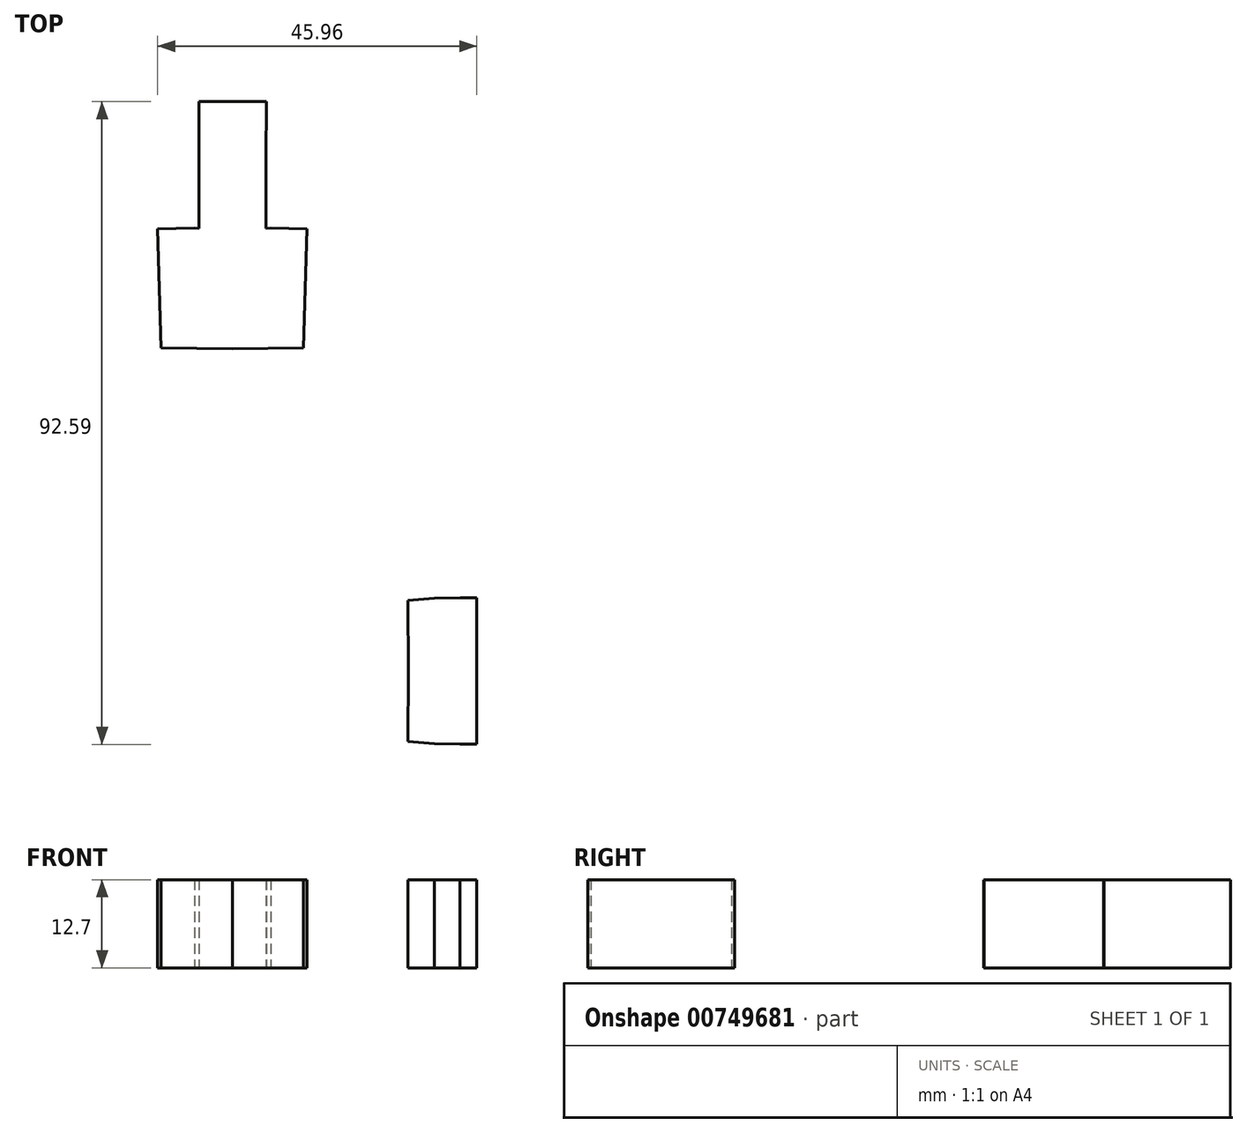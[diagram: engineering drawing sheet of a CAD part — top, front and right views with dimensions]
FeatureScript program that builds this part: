
annotation { "Feature Type Name" : "Feature", "Feature Type Description" : "" }
export const myFeature = defineFeature(function(context is Context, id is Id, definition is map)
    precondition{}
    {
        {
            var Q0;
            Q0=qCreatedBy(makeId("Top.planeOp"),FACE);
            var sketch = newSketch(context, id + "F0", { "sketchPlane" : qUnion([Q0])});
            skLineSegment(sketch, "E0", {"start": v(-36.51, 121.34) * mm, "end": v(-36.27, 119.16) * mm});
            skLineSegment(sketch, "E1", {"start": v(-36.07, 123.48) * mm, "end": v(-36.51, 121.34) * mm});
            skLineSegment(sketch, "E2", {"start": v(-29.86, 114.03) * mm, "end": v(-27.69, 114.27) * mm});
            skLineSegment(sketch, "E3", {"start": v(-27.69, 114.27) * mm, "end": v(-25.7, 115.16) * mm});
            skLineSegment(sketch, "E4", {"start": v(-33.9, 115.55) * mm, "end": v(-32, 114.47) * mm});
            skLineSegment(sketch, "E5", {"start": v(-32, 114.47) * mm, "end": v(-29.86, 114.03) * mm});
            skLineSegment(sketch, "E6", {"start": v(-25.16, 126.46) * mm, "end": v(-27.06, 127.54) * mm});
            skLineSegment(sketch, "E7", {"start": v(-27.06, 127.54) * mm, "end": v(-29.2, 127.99) * mm});
            skLineSegment(sketch, "E8", {"start": v(-22.8, 122.85) * mm, "end": v(-23.69, 124.84) * mm});
            skLineSegment(sketch, "E9", {"start": v(-23.69, 124.84) * mm, "end": v(-25.16, 126.46) * mm});
            skLineSegment(sketch, "E10", {"start": v(-33.37, 126.85) * mm, "end": v(-34.98, 125.38) * mm});
            skLineSegment(sketch, "E11", {"start": v(-34.98, 125.38) * mm, "end": v(-36.07, 123.48) * mm});
            skLineSegment(sketch, "E12", {"start": v(-29.2, 127.99) * mm, "end": v(-31.37, 127.75) * mm});
            skLineSegment(sketch, "E13", {"start": v(-31.37, 127.75) * mm, "end": v(-33.37, 126.85) * mm});
            skLineSegment(sketch, "E14", {"start": v(-23, 118.53) * mm, "end": v(-22.55, 120.67) * mm});
            skLineSegment(sketch, "E15", {"start": v(-22.55, 120.67) * mm, "end": v(-22.8, 122.85) * mm});
            skLineSegment(sketch, "E16", {"start": v(-25.7, 115.16) * mm, "end": v(-24.08, 116.64) * mm});
            skLineSegment(sketch, "E17", {"start": v(-24.08, 116.64) * mm, "end": v(-23, 118.53) * mm});
            skLineSegment(sketch, "E18", {"start": v(-36.27, 119.16) * mm, "end": v(-35.37, 117.17) * mm});
            skLineSegment(sketch, "E19", {"start": v(-35.37, 117.17) * mm, "end": v(-33.9, 115.55) * mm});
            skLineSegment(sketch, "E20", {"start": v(-21.43, 123.46) * mm, "end": v(-22.32, 125.46) * mm});
            skLineSegment(sketch, "E21", {"start": v(-20.53, 121.47) * mm, "end": v(-21.43, 123.46) * mm});
            skLineSegment(sketch, "E22", {"start": v(-19.9, 119.28) * mm, "end": v(-20.53, 121.47) * mm});
            skLineSegment(sketch, "E23", {"start": v(-39.23, 123.54) * mm, "end": v(-40.65, 122.6) * mm});
            skLineSegment(sketch, "E24", {"start": v(-57.32, -66.74) * mm, "end": v(-57.32, -74.04) * mm});
            skLineSegment(sketch, "E25", {"start": v(-57.32, -74.04) * mm, "end": v(-57.32, -81.34) * mm});
            skLineSegment(sketch, "E26", {"start": v(-57.32, -81.34) * mm, "end": v(-50.68, -80.7) * mm});
            skLineSegment(sketch, "E27", {"start": v(-39.13, -68.41) * mm, "end": v(-50.68, -67.38) * mm});
            skLineSegment(sketch, "E28", {"start": v(-50.68, -67.38) * mm, "end": v(-57.32, -66.74) * mm});
            skLineSegment(sketch, "E29", {"start": v(-50.68, -80.7) * mm, "end": v(-39.38, -79.55) * mm});
            skLineSegment(sketch, "E30", {"start": v(-40.45, -82.84) * mm, "end": v(-39.38, -79.55) * mm});
            skLineSegment(sketch, "E31", {"start": v(-51.06, -83.72) * mm, "end": v(-40.45, -82.84) * mm});
            skLineSegment(sketch, "E32", {"start": v(-57.32, -81.34) * mm, "end": v(-57.63, -84.23) * mm});
            skLineSegment(sketch, "E33", {"start": v(-57.63, -63.85) * mm, "end": v(-57.32, -66.74) * mm});
            skLineSegment(sketch, "E34", {"start": v(-40.45, -65.23) * mm, "end": v(-51.06, -64.36) * mm});
            skLineSegment(sketch, "E35", {"start": v(-39.13, -68.41) * mm, "end": v(-40.45, -65.23) * mm});
            skLineSegment(sketch, "E36", {"start": v(-41.05, -87.72) * mm, "end": v(-39.4, -84.97) * mm});
            skLineSegment(sketch, "E37", {"start": v(-39.4, -84.97) * mm, "end": v(-40.45, -82.84) * mm});
            skLineSegment(sketch, "E38", {"start": v(-51.43, -85.25) * mm, "end": v(-41.05, -87.72) * mm});
            skLineSegment(sketch, "E39", {"start": v(-57.63, -84.2) * mm, "end": v(-51.43, -85.25) * mm});
            skLineSegment(sketch, "E40", {"start": v(-51.06, -83.72) * mm, "end": v(-57.63, -84.2) * mm});
            skLineSegment(sketch, "E41", {"start": v(-40.45, -65.23) * mm, "end": v(-39.4, -63.1) * mm});
            skLineSegment(sketch, "E42", {"start": v(-39.4, -63.1) * mm, "end": v(-41.05, -60.35) * mm});
            skLineSegment(sketch, "E43", {"start": v(-41.05, -60.35) * mm, "end": v(-51.43, -62.82) * mm});
            skLineSegment(sketch, "E44", {"start": v(-57.63, -63.88) * mm, "end": v(-51.06, -64.36) * mm});
            skLineSegment(sketch, "E45", {"start": v(-51.43, -62.82) * mm, "end": v(-57.63, -63.88) * mm});
            skLineSegment(sketch, "E46", {"start": v(-36.61, -76.89) * mm, "end": v(-37.07, -74.03) * mm});
            skLineSegment(sketch, "E47", {"start": v(-33.46, -77.71) * mm, "end": v(-36.61, -76.89) * mm});
            skLineSegment(sketch, "E48", {"start": v(-24.1, -74.32) * mm, "end": v(-24.17, -77.93) * mm});
            skLineSegment(sketch, "E49", {"start": v(-33.5, -79.68) * mm, "end": v(-22.06, -79.95) * mm});
            skLineSegment(sketch, "E50", {"start": v(-24.17, -77.93) * mm, "end": v(-33.46, -77.71) * mm});
            skLineSegment(sketch, "E51", {"start": v(-37.07, -74.03) * mm, "end": v(-36.48, -71.2) * mm});
            skLineSegment(sketch, "E52", {"start": v(-36.48, -71.2) * mm, "end": v(-33.3, -70.51) * mm});
            skLineSegment(sketch, "E53", {"start": v(-24, -70.72) * mm, "end": v(-24.1, -74.32) * mm});
            skLineSegment(sketch, "E54", {"start": v(-33.3, -70.51) * mm, "end": v(-24, -70.72) * mm});
            skLineSegment(sketch, "E55", {"start": v(-21.8, -68.8) * mm, "end": v(-33.25, -68.54) * mm});
            skLineSegment(sketch, "E56", {"start": v(-39.38, -79.55) * mm, "end": v(-37.63, -82.46) * mm});
            skLineSegment(sketch, "E57", {"start": v(-20.94, -91.92) * mm, "end": v(-23.48, -82.8) * mm});
            skLineSegment(sketch, "E58", {"start": v(-35.26, -82.54) * mm, "end": v(-28.7, -91.67) * mm});
            skLineSegment(sketch, "E59", {"start": v(-37.63, -82.46) * mm, "end": v(-35.26, -82.54) * mm});
            skLineSegment(sketch, "E60", {"start": v(-23.48, -82.8) * mm, "end": v(-22.06, -79.95) * mm});
            skLineSegment(sketch, "E61", {"start": v(-37.25, -65.58) * mm, "end": v(-39.13, -68.4) * mm});
            skLineSegment(sketch, "E62", {"start": v(-23.1, -65.87) * mm, "end": v(-20.15, -56.89) * mm});
            skLineSegment(sketch, "E63", {"start": v(-27.92, -56.79) * mm, "end": v(-34.87, -65.6) * mm});
            skLineSegment(sketch, "E64", {"start": v(-34.87, -65.6) * mm, "end": v(-37.25, -65.58) * mm});
            skLineSegment(sketch, "E65", {"start": v(-20.15, -56.89) * mm, "end": v(-27.92, -56.79) * mm});
            skLineSegment(sketch, "E66", {"start": v(-21.8, -68.8) * mm, "end": v(-23.1, -65.87) * mm});
            skLineSegment(sketch, "E67", {"start": v(-26.5, -43.73) * mm, "end": v(-27.92, -56.79) * mm});
            skLineSegment(sketch, "E68", {"start": v(-25.3, -32.83) * mm, "end": v(-26.5, -43.73) * mm});
            skLineSegment(sketch, "E69", {"start": v(-28.7, -91.67) * mm, "end": v(-27.88, -104.78) * mm});
            skLineSegment(sketch, "E70", {"start": v(-21.6, -106.6) * mm, "end": v(-20.94, -91.92) * mm});
            skLineSegment(sketch, "E71", {"start": v(-22.05, -116.27) * mm, "end": v(-21.6, -106.6) * mm});
            skLineSegment(sketch, "E72", {"start": v(-27.88, -104.78) * mm, "end": v(-27.18, -115.72) * mm});
            skLineSegment(sketch, "E73", {"start": v(-28.91, -126.27) * mm, "end": v(-23.98, -129.47) * mm});
            skLineSegment(sketch, "E74", {"start": v(-23.98, -129.47) * mm, "end": v(-22.05, -116.27) * mm});
            skLineSegment(sketch, "E75", {"start": v(-20.15, -42.2) * mm, "end": v(-20.14, -32.5) * mm});
            skLineSegment(sketch, "E76", {"start": v(-20.15, -56.89) * mm, "end": v(-20.15, -42.2) * mm});
            skLineSegment(sketch, "E77", {"start": v(-21.47, -19.24) * mm, "end": v(-26.55, -22.22) * mm});
            skLineSegment(sketch, "E78", {"start": v(-26.55, -22.22) * mm, "end": v(-25.3, -32.83) * mm});
            skLineSegment(sketch, "E79", {"start": v(-20.14, -32.5) * mm, "end": v(-21.47, -19.24) * mm});
            skLineSegment(sketch, "E80", {"start": v(-20.2, -66.03) * mm, "end": v(-21.8, -68.8) * mm});
            skLineSegment(sketch, "E81", {"start": v(-21.8, -68.8) * mm, "end": v(-13.28, -69.7) * mm});
            skLineSegment(sketch, "E82", {"start": v(-8.5, -69.93) * mm, "end": v(-13.28, -69.7) * mm});
            skLineSegment(sketch, "E83", {"start": v(-3.9, -70.15) * mm, "end": v(-8.5, -69.93) * mm});
            skLineSegment(sketch, "E84", {"start": v(-13.77, -79.86) * mm, "end": v(-8.99, -80.09) * mm});
            skLineSegment(sketch, "E85", {"start": v(-8.99, -80.09) * mm, "end": v(-4.39, -80.3) * mm});
            skLineSegment(sketch, "E86", {"start": v(-22.06, -79.95) * mm, "end": v(-13.77, -79.86) * mm});
            skLineSegment(sketch, "E87", {"start": v(-4.39, -80.3) * mm, "end": v(-4.14, -75.23) * mm});
            skLineSegment(sketch, "E88", {"start": v(-4.14, -75.23) * mm, "end": v(-3.9, -70.15) * mm});
            skLineSegment(sketch, "E89", {"start": v(-22.06, -79.95) * mm, "end": v(-21.01, -82.84) * mm});
            skLineSegment(sketch, "E90", {"start": v(-21.01, -82.84) * mm, "end": v(-14.18, -82.29) * mm});
            skLineSegment(sketch, "E91", {"start": v(-13.46, -67.24) * mm, "end": v(-20.2, -66.03) * mm});
            skLineSegment(sketch, "E92", {"start": v(-3.9, -70.15) * mm, "end": v(-3.76, -68.34) * mm});
            skLineSegment(sketch, "E93", {"start": v(-3.76, -68.34) * mm, "end": v(-8.26, -68) * mm});
            skLineSegment(sketch, "E94", {"start": v(-8.25, -68) * mm, "end": v(-13.46, -67.24) * mm});
            skLineSegment(sketch, "E95", {"start": v(-14.32, -82.26) * mm, "end": v(-8.92, -82.04) * mm});
            skLineSegment(sketch, "E96", {"start": v(-8.93, -82.04) * mm, "end": v(-4.42, -82.12) * mm});
            skLineSegment(sketch, "E97", {"start": v(-4.42, -82.12) * mm, "end": v(-4.39, -80.3) * mm});
            skLineSegment(sketch, "E98", {"start": v(37.47, -31.88) * mm, "end": v(29.33, -34.66) * mm});
            skLineSegment(sketch, "E99", {"start": v(21.15, -37.5) * mm, "end": v(17.9, -38.24) * mm});
            skLineSegment(sketch, "E100", {"start": v(19.54, -40.65) * mm, "end": v(20.83, -42.47) * mm});
            skLineSegment(sketch, "E101", {"start": v(29.33, -34.66) * mm, "end": v(21.15, -37.5) * mm});
            skLineSegment(sketch, "E102", {"start": v(30.83, -39.06) * mm, "end": v(38.98, -36.28) * mm});
            skLineSegment(sketch, "E103", {"start": v(20.83, -42.47) * mm, "end": v(30.83, -39.06) * mm});
            skLineSegment(sketch, "E104", {"start": v(1.77, -57.6) * mm, "end": v(1.1, -53.99) * mm});
            skLineSegment(sketch, "E105", {"start": v(8.75, -51.24) * mm, "end": v(8.5, -48.14) * mm});
            skLineSegment(sketch, "E106", {"start": v(1.1, -53.99) * mm, "end": v(4.13, -55.44) * mm});
            skLineSegment(sketch, "E107", {"start": v(4.13, -55.44) * mm, "end": v(8.75, -51.24) * mm});
            skLineSegment(sketch, "E108", {"start": v(11.25, -49.23) * mm, "end": v(20.83, -42.47) * mm});
            skLineSegment(sketch, "E109", {"start": v(17.9, -38.24) * mm, "end": v(6.8, -45.73) * mm});
            skLineSegment(sketch, "E110", {"start": v(8.5, -48.14) * mm, "end": v(11.25, -49.23) * mm});
            skLineSegment(sketch, "E111", {"start": v(6.8, -45.73) * mm, "end": v(-1.16, -51.27) * mm});
            skLineSegment(sketch, "E112", {"start": v(-1.16, -51.27) * mm, "end": v(-13.2, -59.66) * mm});
            skLineSegment(sketch, "E113", {"start": v(-7.17, -65.03) * mm, "end": v(-3.76, -68.34) * mm});
            skLineSegment(sketch, "E114", {"start": v(-3.76, -68.34) * mm, "end": v(-2.88, -61.83) * mm});
            skLineSegment(sketch, "E115", {"start": v(-13.46, -67.24) * mm, "end": v(-7.17, -65.03) * mm});
            skLineSegment(sketch, "E116", {"start": v(-2.88, -61.83) * mm, "end": v(1.77, -57.6) * mm});
            skLineSegment(sketch, "E117", {"start": v(19.54, -40.65) * mm, "end": v(17.85, -38.26) * mm});
            skLineSegment(sketch, "E118", {"start": v(38.98, -36.28) * mm, "end": v(38.28, -34.26) * mm});
            skLineSegment(sketch, "E119", {"start": v(38.28, -34.26) * mm, "end": v(37.47, -31.88) * mm});
            skLineSegment(sketch, "E120", {"start": v(17.57, -110.23) * mm, "end": v(16.11, -111.92) * mm});
            skLineSegment(sketch, "E121", {"start": v(14.2, -114.14) * mm, "end": v(17.42, -115.21) * mm});
            skLineSegment(sketch, "E122", {"start": v(17.42, -115.21) * mm, "end": v(25.28, -118.82) * mm});
            skLineSegment(sketch, "E123", {"start": v(25.28, -118.82) * mm, "end": v(33.12, -122.37) * mm});
            skLineSegment(sketch, "E124", {"start": v(34.16, -120.08) * mm, "end": v(35.04, -118.13) * mm});
            skLineSegment(sketch, "E125", {"start": v(33.12, -122.37) * mm, "end": v(34.16, -120.08) * mm});
            skLineSegment(sketch, "E126", {"start": v(27.2, -114.59) * mm, "end": v(17.57, -110.23) * mm});
            skLineSegment(sketch, "E127", {"start": v(35.04, -118.13) * mm, "end": v(27.2, -114.59) * mm});
            skLineSegment(sketch, "E128", {"start": v(-0.96, -96.88) * mm, "end": v(0.05, -93.35) * mm});
            skLineSegment(sketch, "E129", {"start": v(0.05, -93.35) * mm, "end": v(-4.17, -88.69) * mm});
            skLineSegment(sketch, "E130", {"start": v(-8.94, -89.22) * mm, "end": v(-14.66, -89.85) * mm});
            skLineSegment(sketch, "E131", {"start": v(5.85, -103.4) * mm, "end": v(6.39, -100.35) * mm});
            skLineSegment(sketch, "E132", {"start": v(6.39, -100.35) * mm, "end": v(2.2, -95.72) * mm});
            skLineSegment(sketch, "E133", {"start": v(-4.17, -88.7) * mm, "end": v(-4.27, -82.08) * mm});
            skLineSegment(sketch, "E134", {"start": v(-4.27, -82.08) * mm, "end": v(-8.78, -82.18) * mm});
            skLineSegment(sketch, "E135", {"start": v(-21.01, -82.84) * mm, "end": v(-14.66, -89.85) * mm});
            skLineSegment(sketch, "E136", {"start": v(-8.78, -82.18) * mm, "end": v(-14.18, -82.29) * mm});
            skLineSegment(sketch, "E137", {"start": v(8.68, -102.59) * mm, "end": v(5.85, -103.4) * mm});
            skLineSegment(sketch, "E138", {"start": v(17.57, -110.23) * mm, "end": v(8.68, -102.59) * mm});
            skLineSegment(sketch, "E139", {"start": v(3.92, -105.64) * mm, "end": v(14.2, -114.14) * mm});
            skLineSegment(sketch, "E140", {"start": v(14.2, -114.14) * mm, "end": v(16.11, -111.92) * mm});
            skLineSegment(sketch, "E141", {"start": v(-26.98, -9.24) * mm, "end": v(-24.98, -8.22) * mm});
            skLineSegment(sketch, "E142", {"start": v(-24.98, -8.22) * mm, "end": v(-23.4, -6.64) * mm});
            skLineSegment(sketch, "E143", {"start": v(-36.35, -2.43) * mm, "end": v(-36, -4.64) * mm});
            skLineSegment(sketch, "E144", {"start": v(-36, -4.64) * mm, "end": v(-34.99, -6.64) * mm});
            skLineSegment(sketch, "E145", {"start": v(-34.99, 1.78) * mm, "end": v(-36, -0.21) * mm});
            skLineSegment(sketch, "E146", {"start": v(-36, -0.21) * mm, "end": v(-36.35, -2.43) * mm});
            skLineSegment(sketch, "E147", {"start": v(-23.4, 1.78) * mm, "end": v(-24.98, 3.37) * mm});
            skLineSegment(sketch, "E148", {"start": v(-24.98, 3.37) * mm, "end": v(-26.98, 4.39) * mm});
            skLineSegment(sketch, "E149", {"start": v(-22.03, -2.43) * mm, "end": v(-22.38, -0.21) * mm});
            skLineSegment(sketch, "E150", {"start": v(-22.38, -0.21) * mm, "end": v(-23.4, 1.78) * mm});
            skLineSegment(sketch, "E151", {"start": v(-31.4, 4.39) * mm, "end": v(-33.4, 3.37) * mm});
            skLineSegment(sketch, "E152", {"start": v(-33.4, 3.37) * mm, "end": v(-34.99, 1.78) * mm});
            skLineSegment(sketch, "E153", {"start": v(-26.98, 4.39) * mm, "end": v(-29.2, 4.74) * mm});
            skLineSegment(sketch, "E154", {"start": v(-29.2, 4.74) * mm, "end": v(-31.4, 4.39) * mm});
            skLineSegment(sketch, "E155", {"start": v(-34.99, -6.64) * mm, "end": v(-33.4, -8.22) * mm});
            skLineSegment(sketch, "E156", {"start": v(-33.4, -8.22) * mm, "end": v(-31.4, -9.24) * mm});
            skLineSegment(sketch, "E157", {"start": v(-23.4, -6.64) * mm, "end": v(-22.38, -4.64) * mm});
            skLineSegment(sketch, "E158", {"start": v(-22.38, -4.64) * mm, "end": v(-22.03, -2.43) * mm});
            skLineSegment(sketch, "E159", {"start": v(-34.39, -10.16) * mm, "end": v(-32.4, -11.18) * mm});
            skLineSegment(sketch, "E160", {"start": v(-31.4, -9.24) * mm, "end": v(-29.2, -9.59) * mm});
            skLineSegment(sketch, "E161", {"start": v(-29.2, -9.59) * mm, "end": v(-26.98, -9.24) * mm});
            skLineSegment(sketch, "E162", {"start": v(-31.75, -11.39) * mm, "end": v(-29.53, -11.74) * mm});
            skLineSegment(sketch, "E163", {"start": v(-28.85, -11.74) * mm, "end": v(-26.64, -11.39) * mm});
            skLineSegment(sketch, "E164", {"start": v(-36.52, -8.17) * mm, "end": v(-34.94, -9.76) * mm});
            skLineSegment(sketch, "E165", {"start": v(-38.1, -6.59) * mm, "end": v(-36.52, -8.17) * mm});
            skLineSegment(sketch, "E166", {"start": v(-39.7, -5) * mm, "end": v(-38.1, -6.59) * mm});
            skLineSegment(sketch, "E167", {"start": v(-26, -11.18) * mm, "end": v(-24, -10.16) * mm});
            skLineSegment(sketch, "E168", {"start": v(-23.44, -9.76) * mm, "end": v(-21.86, -8.17) * mm});
            skLineSegment(sketch, "E169", {"start": v(-21.46, -7.62) * mm, "end": v(-20.44, -5.63) * mm});
            skLineSegment(sketch, "E170", {"start": v(-19.88, -2.77) * mm, "end": v(-19.9, -0.74) * mm});
            skLineSegment(sketch, "E171", {"start": v(-20.23, -4.98) * mm, "end": v(-19.88, -2.77) * mm});
            skLineSegment(sketch, "E172", {"start": v(46.13, 58.02) * mm, "end": v(57.33, 58.02) * mm});
            skLineSegment(sketch, "E173", {"start": v(46.13, 65.4) * mm, "end": v(46.13, 58.02) * mm});
            skLineSegment(sketch, "E174", {"start": v(46.13, 58.02) * mm, "end": v(52.12, 50.91) * mm});
            skLineSegment(sketch, "E175", {"start": v(52.12, 50.91) * mm, "end": v(58.94, 50.91) * mm});
            skLineSegment(sketch, "E176", {"start": v(58.94, 50.91) * mm, "end": v(57.33, 58.02) * mm});
            skLineSegment(sketch, "E177", {"start": v(57.33, 58.02) * mm, "end": v(57.33, 65.4) * mm});
            skLineSegment(sketch, "E178", {"start": v(57.33, 72.8) * mm, "end": v(46.13, 72.8) * mm});
            skLineSegment(sketch, "E179", {"start": v(46.13, 72.8) * mm, "end": v(46.13, 65.4) * mm});
            skLineSegment(sketch, "E180", {"start": v(52.12, 79.9) * mm, "end": v(46.13, 72.8) * mm});
            skLineSegment(sketch, "E181", {"start": v(57.33, 72.8) * mm, "end": v(58.94, 79.9) * mm});
            skLineSegment(sketch, "E182", {"start": v(58.94, 79.9) * mm, "end": v(52.12, 79.9) * mm});
            skLineSegment(sketch, "E183", {"start": v(57.33, 65.4) * mm, "end": v(57.33, 72.8) * mm});
            skLineSegment(sketch, "E184", {"start": v(31, 102.69) * mm, "end": v(25.18, 95.62) * mm});
            skLineSegment(sketch, "E185", {"start": v(25.18, 95.62) * mm, "end": v(31.99, 88.2) * mm});
            skLineSegment(sketch, "E186", {"start": v(38.8, 80.78) * mm, "end": v(46.13, 72.8) * mm});
            skLineSegment(sketch, "E187", {"start": v(52.12, 79.9) * mm, "end": v(45.38, 87.33) * mm});
            skLineSegment(sketch, "E188", {"start": v(31.99, 88.2) * mm, "end": v(38.8, 80.78) * mm});
            skLineSegment(sketch, "E189", {"start": v(45.38, 43.49) * mm, "end": v(52.12, 50.91) * mm});
            skLineSegment(sketch, "E190", {"start": v(25.18, 35.2) * mm, "end": v(31, 28.14) * mm});
            skLineSegment(sketch, "E191", {"start": v(46.13, 58.02) * mm, "end": v(38.8, 50.03) * mm});
            skLineSegment(sketch, "E192", {"start": v(38.8, 50.03) * mm, "end": v(31.99, 42.61) * mm});
            skLineSegment(sketch, "E193", {"start": v(31.99, 42.61) * mm, "end": v(25.18, 35.2) * mm});
            skLineSegment(sketch, "E194", {"start": v(35.38, 71.74) * mm, "end": v(35.38, 65.4) * mm});
            skLineSegment(sketch, "E195", {"start": v(25.4, 55.26) * mm, "end": v(35.38, 56.59) * mm});
            skLineSegment(sketch, "E196", {"start": v(35.38, 59.07) * mm, "end": v(25.4, 59.07) * mm});
            skLineSegment(sketch, "E197", {"start": v(15.42, 59.07) * mm, "end": v(15.42, 53.93) * mm});
            skLineSegment(sketch, "E198", {"start": v(15.42, 53.93) * mm, "end": v(25.4, 55.26) * mm});
            skLineSegment(sketch, "E199", {"start": v(25.4, 59.07) * mm, "end": v(15.42, 59.07) * mm});
            skLineSegment(sketch, "E200", {"start": v(35.38, 56.59) * mm, "end": v(46.13, 58.02) * mm});
            skLineSegment(sketch, "E201", {"start": v(35.38, 65.4) * mm, "end": v(35.38, 59.07) * mm});
            skLineSegment(sketch, "E202", {"start": v(25.4, 71.74) * mm, "end": v(35.38, 71.74) * mm});
            skLineSegment(sketch, "E203", {"start": v(15.42, 71.74) * mm, "end": v(25.4, 71.74) * mm});
            skLineSegment(sketch, "E204", {"start": v(15.42, 76.88) * mm, "end": v(15.42, 71.74) * mm});
            skLineSegment(sketch, "E205", {"start": v(46.13, 72.8) * mm, "end": v(35.38, 74.22) * mm});
            skLineSegment(sketch, "E206", {"start": v(35.38, 74.22) * mm, "end": v(25.4, 75.55) * mm});
            skLineSegment(sketch, "E207", {"start": v(25.4, 75.55) * mm, "end": v(15.42, 76.88) * mm});
            skLineSegment(sketch, "E208", {"start": v(45.38, 87.33) * mm, "end": v(39.04, 94.25) * mm});
            skLineSegment(sketch, "E209", {"start": v(36.73, 109.95) * mm, "end": v(30.9, 102.8) * mm});
            skLineSegment(sketch, "E210", {"start": v(30.9, 102.8) * mm, "end": v(39.04, 94.25) * mm});
            skLineSegment(sketch, "E211", {"start": v(46.07, 112.22) * mm, "end": v(43.84, 112.01) * mm});
            skLineSegment(sketch, "E212", {"start": v(43.84, 112.01) * mm, "end": v(41.65, 112.5) * mm});
            skLineSegment(sketch, "E213", {"start": v(41.65, 112.5) * mm, "end": v(39.72, 113.64) * mm});
            skLineSegment(sketch, "E214", {"start": v(39.72, 113.64) * mm, "end": v(38.24, 115.32) * mm});
            skLineSegment(sketch, "E215", {"start": v(35, 116.78) * mm, "end": v(36.73, 109.95) * mm});
            skLineSegment(sketch, "E216", {"start": v(38.24, 115.32) * mm, "end": v(37.35, 117.38) * mm});
            skLineSegment(sketch, "E217", {"start": v(37.35, 117.38) * mm, "end": v(37.14, 119.61) * mm});
            skLineSegment(sketch, "E218", {"start": v(34.72, 119.76) * mm, "end": v(35, 116.78) * mm});
            skLineSegment(sketch, "E219", {"start": v(37.14, 119.61) * mm, "end": v(37.63, 121.8) * mm});
            skLineSegment(sketch, "E220", {"start": v(35.37, 122.69) * mm, "end": v(34.72, 119.76) * mm});
            skLineSegment(sketch, "E221", {"start": v(37.63, 121.8) * mm, "end": v(38.77, 123.73) * mm});
            skLineSegment(sketch, "E222", {"start": v(36.9, 125.27) * mm, "end": v(35.37, 122.69) * mm});
            skLineSegment(sketch, "E223", {"start": v(38.77, 123.73) * mm, "end": v(40.45, 125.21) * mm});
            skLineSegment(sketch, "E224", {"start": v(39.15, 127.26) * mm, "end": v(36.9, 125.27) * mm});
            skLineSegment(sketch, "E225", {"start": v(40.45, 125.21) * mm, "end": v(42.5, 126.1) * mm});
            skLineSegment(sketch, "E226", {"start": v(41.9, 128.45) * mm, "end": v(39.15, 127.26) * mm});
            skLineSegment(sketch, "E227", {"start": v(42.5, 126.1) * mm, "end": v(44.73, 126.32) * mm});
            skLineSegment(sketch, "E228", {"start": v(44.88, 128.74) * mm, "end": v(41.9, 128.45) * mm});
            skLineSegment(sketch, "E229", {"start": v(47.81, 128.09) * mm, "end": v(44.88, 128.74) * mm});
            skLineSegment(sketch, "E230", {"start": v(44.73, 126.32) * mm, "end": v(46.92, 125.83) * mm});
            skLineSegment(sketch, "E231", {"start": v(50.4, 126.56) * mm, "end": v(47.81, 128.09) * mm});
            skLineSegment(sketch, "E232", {"start": v(46.92, 125.83) * mm, "end": v(48.85, 124.7) * mm});
            skLineSegment(sketch, "E233", {"start": v(48.85, 124.7) * mm, "end": v(50.34, 123.01) * mm});
            skLineSegment(sketch, "E234", {"start": v(52.38, 124.31) * mm, "end": v(50.4, 126.56) * mm});
            skLineSegment(sketch, "E235", {"start": v(50.34, 123.01) * mm, "end": v(51.23, 120.96) * mm});
            skLineSegment(sketch, "E236", {"start": v(53.58, 121.56) * mm, "end": v(52.38, 124.31) * mm});
            skLineSegment(sketch, "E237", {"start": v(51.23, 120.96) * mm, "end": v(51.44, 118.73) * mm});
            skLineSegment(sketch, "E238", {"start": v(57.54, 103.91) * mm, "end": v(53.58, 121.56) * mm});
            skLineSegment(sketch, "E239", {"start": v(51.44, 118.73) * mm, "end": v(50.96, 116.54) * mm});
            skLineSegment(sketch, "E240", {"start": v(50.96, 116.54) * mm, "end": v(49.82, 114.6) * mm});
            skLineSegment(sketch, "E241", {"start": v(49.82, 114.6) * mm, "end": v(48.14, 113.12) * mm});
            skLineSegment(sketch, "E242", {"start": v(48.14, 113.12) * mm, "end": v(46.07, 112.22) * mm});
            skLineSegment(sketch, "E243", {"start": v(58.77, 81.44) * mm, "end": v(57.54, 103.91) * mm});
            skLineSegment(sketch, "E244", {"start": v(52.12, 79.9) * mm, "end": v(58.77, 81.44) * mm});
            skLineSegment(sketch, "E245", {"start": v(46.08, 18.58) * mm, "end": v(48.14, 17.69) * mm});
            skLineSegment(sketch, "E246", {"start": v(48.14, 17.69) * mm, "end": v(49.82, 16.2) * mm});
            skLineSegment(sketch, "E247", {"start": v(49.82, 16.2) * mm, "end": v(50.96, 14.27) * mm});
            skLineSegment(sketch, "E248", {"start": v(50.96, 14.27) * mm, "end": v(51.44, 12.09) * mm});
            skLineSegment(sketch, "E249", {"start": v(51.44, 12.09) * mm, "end": v(51.23, 9.86) * mm});
            skLineSegment(sketch, "E250", {"start": v(53.58, 9.25) * mm, "end": v(57.53, 26.98) * mm});
            skLineSegment(sketch, "E251", {"start": v(51.23, 9.86) * mm, "end": v(50.34, 7.8) * mm});
            skLineSegment(sketch, "E252", {"start": v(52.38, 6.5) * mm, "end": v(53.58, 9.25) * mm});
            skLineSegment(sketch, "E253", {"start": v(50.34, 7.8) * mm, "end": v(48.85, 6.12) * mm});
            skLineSegment(sketch, "E254", {"start": v(50.4, 4.25) * mm, "end": v(52.38, 6.5) * mm});
            skLineSegment(sketch, "E255", {"start": v(48.85, 6.12) * mm, "end": v(46.92, 4.98) * mm});
            skLineSegment(sketch, "E256", {"start": v(47.81, 2.73) * mm, "end": v(50.4, 4.25) * mm});
            skLineSegment(sketch, "E257", {"start": v(46.92, 4.98) * mm, "end": v(44.73, 4.5) * mm});
            skLineSegment(sketch, "E258", {"start": v(44.88, 2.08) * mm, "end": v(47.81, 2.73) * mm});
            skLineSegment(sketch, "E259", {"start": v(44.73, 4.5) * mm, "end": v(42.5, 4.7) * mm});
            skLineSegment(sketch, "E260", {"start": v(41.9, 2.36) * mm, "end": v(44.88, 2.08) * mm});
            skLineSegment(sketch, "E261", {"start": v(42.5, 4.7) * mm, "end": v(40.45, 5.6) * mm});
            skLineSegment(sketch, "E262", {"start": v(39.15, 3.55) * mm, "end": v(41.9, 2.36) * mm});
            skLineSegment(sketch, "E263", {"start": v(40.45, 5.6) * mm, "end": v(38.77, 7.08) * mm});
            skLineSegment(sketch, "E264", {"start": v(36.9, 5.54) * mm, "end": v(39.15, 3.55) * mm});
            skLineSegment(sketch, "E265", {"start": v(38.77, 7.08) * mm, "end": v(37.63, 9.01) * mm});
            skLineSegment(sketch, "E266", {"start": v(35.37, 8.12) * mm, "end": v(36.9, 5.54) * mm});
            skLineSegment(sketch, "E267", {"start": v(37.63, 9.01) * mm, "end": v(37.14, 11.2) * mm});
            skLineSegment(sketch, "E268", {"start": v(34.72, 11.05) * mm, "end": v(35.37, 8.12) * mm});
            skLineSegment(sketch, "E269", {"start": v(37.14, 11.2) * mm, "end": v(37.35, 13.43) * mm});
            skLineSegment(sketch, "E270", {"start": v(35, 14.04) * mm, "end": v(34.72, 11.05) * mm});
            skLineSegment(sketch, "E271", {"start": v(37.35, 13.43) * mm, "end": v(38.24, 15.49) * mm});
            skLineSegment(sketch, "E272", {"start": v(36.73, 20.86) * mm, "end": v(35, 14.04) * mm});
            skLineSegment(sketch, "E273", {"start": v(38.24, 15.49) * mm, "end": v(39.72, 17.17) * mm});
            skLineSegment(sketch, "E274", {"start": v(39.72, 17.17) * mm, "end": v(41.65, 18.3) * mm});
            skLineSegment(sketch, "E275", {"start": v(41.65, 18.3) * mm, "end": v(43.84, 18.8) * mm});
            skLineSegment(sketch, "E276", {"start": v(43.84, 18.8) * mm, "end": v(46.08, 18.58) * mm});
            skLineSegment(sketch, "E277", {"start": v(39.12, 36.6) * mm, "end": v(30.93, 28.2) * mm});
            skLineSegment(sketch, "E278", {"start": v(30.93, 28.2) * mm, "end": v(36.73, 20.86) * mm});
            skLineSegment(sketch, "E279", {"start": v(57.53, 26.98) * mm, "end": v(58.77, 49.38) * mm});
            skLineSegment(sketch, "E280", {"start": v(58.77, 49.38) * mm, "end": v(52.12, 50.91) * mm});
            skLineSegment(sketch, "E281", {"start": v(45.38, 43.49) * mm, "end": v(39.12, 36.6) * mm});
            skLineSegment(sketch, "E282", {"start": v(14.27, 6.42) * mm, "end": v(14.27, -3.46) * mm});
            skLineSegment(sketch, "E283", {"start": v(14.27, 14.78) * mm, "end": v(14.27, 6.42) * mm});
            skLineSegment(sketch, "E284", {"start": v(19.11, 14.78) * mm, "end": v(14.27, 14.78) * mm});
            skLineSegment(sketch, "E285", {"start": v(12.16, 6.61) * mm, "end": v(12.16, -3.37) * mm});
            skLineSegment(sketch, "E286", {"start": v(12.16, -3.37) * mm, "end": v(14.27, -3.46) * mm});
            skLineSegment(sketch, "E287", {"start": v(19.11, 17.13) * mm, "end": v(12.78, 17.13) * mm});
            skLineSegment(sketch, "E288", {"start": v(12.78, 17.13) * mm, "end": v(14.27, 14.78) * mm});
            skLineSegment(sketch, "E289", {"start": v(14.27, 14.78) * mm, "end": v(12.16, 16.6) * mm});
            skLineSegment(sketch, "E290", {"start": v(12.16, 16.6) * mm, "end": v(12.16, 6.61) * mm});
            skLineSegment(sketch, "E291", {"start": v(26.06, -3.37) * mm, "end": v(26.07, 6.61) * mm});
            skLineSegment(sketch, "E292", {"start": v(23.95, -3.46) * mm, "end": v(23.96, 6.41) * mm});
            skLineSegment(sketch, "E293", {"start": v(23.95, -3.46) * mm, "end": v(26.06, -3.37) * mm});
            skLineSegment(sketch, "E294", {"start": v(23.96, 14.78) * mm, "end": v(25.45, 17.13) * mm});
            skLineSegment(sketch, "E295", {"start": v(25.45, 17.13) * mm, "end": v(19.11, 17.13) * mm});
            skLineSegment(sketch, "E296", {"start": v(23.96, 14.78) * mm, "end": v(19.11, 14.78) * mm});
            skLineSegment(sketch, "E297", {"start": v(23.96, 6.41) * mm, "end": v(23.96, 14.78) * mm});
            skLineSegment(sketch, "E298", {"start": v(26.07, 6.61) * mm, "end": v(26.07, 16.6) * mm});
            skLineSegment(sketch, "E299", {"start": v(26.07, 16.6) * mm, "end": v(23.96, 14.78) * mm});
            skLineSegment(sketch, "E300", {"start": v(44.37, -57.08) * mm, "end": v(44.4, -67.24) * mm});
            skLineSegment(sketch, "E301", {"start": v(51.88, -77.8) * mm, "end": v(54.28, -77.8) * mm});
            skLineSegment(sketch, "E302", {"start": v(54.26, -67.25) * mm, "end": v(54.27, -56.7) * mm});
            skLineSegment(sketch, "E303", {"start": v(54.27, -56.7) * mm, "end": v(51.9, -56.7) * mm});
            skLineSegment(sketch, "E304", {"start": v(48.2, -56.78) * mm, "end": v(44.37, -57.08) * mm});
            skLineSegment(sketch, "E305", {"start": v(51.9, -56.7) * mm, "end": v(48.2, -56.78) * mm});
            skLineSegment(sketch, "E306", {"start": v(44.37, -77.4) * mm, "end": v(48.17, -77.7) * mm});
            skLineSegment(sketch, "E307", {"start": v(54.28, -77.8) * mm, "end": v(54.26, -67.25) * mm});
            skLineSegment(sketch, "E308", {"start": v(48.17, -77.7) * mm, "end": v(51.88, -77.8) * mm});
            skLineSegment(sketch, "E309", {"start": v(44.4, -67.24) * mm, "end": v(44.37, -77.4) * mm});
            skLineSegment(sketch, "E310", {"start": v(48.31, -78.6) * mm, "end": v(44.74, -79.94) * mm});
            skLineSegment(sketch, "E311", {"start": v(55.45, -86.02) * mm, "end": v(54.28, -77.8) * mm});
            skLineSegment(sketch, "E312", {"start": v(44.74, -79.94) * mm, "end": v(45.97, -88.52) * mm});
            skLineSegment(sketch, "E313", {"start": v(49.54, -87) * mm, "end": v(53.16, -86.25) * mm});
            skLineSegment(sketch, "E314", {"start": v(53.16, -86.25) * mm, "end": v(55.45, -86.02) * mm});
            skLineSegment(sketch, "E315", {"start": v(45.97, -88.52) * mm, "end": v(49.54, -87) * mm});
            skLineSegment(sketch, "E316", {"start": v(54.07, -104.07) * mm, "end": v(56.34, -103.06) * mm});
            skLineSegment(sketch, "E317", {"start": v(56.34, -103.06) * mm, "end": v(56, -96.19) * mm});
            skLineSegment(sketch, "E318", {"start": v(56, -96.19) * mm, "end": v(53.52, -93.11) * mm});
            skLineSegment(sketch, "E319", {"start": v(54.68, -115.55) * mm, "end": v(56.94, -114.55) * mm});
            skLineSegment(sketch, "E320", {"start": v(56.57, -107.35) * mm, "end": v(54.07, -104.07) * mm});
            skLineSegment(sketch, "E321", {"start": v(51.04, -115.42) * mm, "end": v(54.68, -115.55) * mm});
            skLineSegment(sketch, "E322", {"start": v(55.78, -92.1) * mm, "end": v(55.45, -86.02) * mm});
            skLineSegment(sketch, "E323", {"start": v(53.52, -93.11) * mm, "end": v(55.78, -92.1) * mm});
            skLineSegment(sketch, "E324", {"start": v(47.56, -114.66) * mm, "end": v(51.04, -115.42) * mm});
            skLineSegment(sketch, "E325", {"start": v(47.02, -105.58) * mm, "end": v(47.56, -114.66) * mm});
            skLineSegment(sketch, "E326", {"start": v(46.5, -95.6) * mm, "end": v(47.02, -105.58) * mm});
            skLineSegment(sketch, "E327", {"start": v(45.97, -88.52) * mm, "end": v(46.5, -95.6) * mm});
            skLineSegment(sketch, "E328", {"start": v(56.94, -114.55) * mm, "end": v(56.57, -107.35) * mm});
            skLineSegment(sketch, "E329", {"start": v(51.9, -77.8) * mm, "end": v(48.31, -78.6) * mm});
            skLineSegment(sketch, "E330", {"start": v(54.27, -56.7) * mm, "end": v(55.43, -48.47) * mm});
            skLineSegment(sketch, "E331", {"start": v(53.13, -48.25) * mm, "end": v(49.52, -47.5) * mm});
            skLineSegment(sketch, "E332", {"start": v(55.43, -48.47) * mm, "end": v(55.75, -42.39) * mm});
            skLineSegment(sketch, "E333", {"start": v(55.75, -42.39) * mm, "end": v(53.49, -41.38) * mm});
            skLineSegment(sketch, "E334", {"start": v(53.49, -41.38) * mm, "end": v(55.96, -38.3) * mm});
            skLineSegment(sketch, "E335", {"start": v(55.96, -38.3) * mm, "end": v(56.3, -31.43) * mm});
            skLineSegment(sketch, "E336", {"start": v(56.3, -31.43) * mm, "end": v(54.03, -30.43) * mm});
            skLineSegment(sketch, "E337", {"start": v(53.13, -48.25) * mm, "end": v(55.43, -48.47) * mm});
            skLineSegment(sketch, "E338", {"start": v(47.5, -19.85) * mm, "end": v(46.98, -28.92) * mm});
            skLineSegment(sketch, "E339", {"start": v(51, -19.08) * mm, "end": v(47.5, -19.85) * mm});
            skLineSegment(sketch, "E340", {"start": v(46.98, -28.92) * mm, "end": v(46.46, -38.9) * mm});
            skLineSegment(sketch, "E341", {"start": v(46.46, -38.9) * mm, "end": v(45.95, -45.98) * mm});
            skLineSegment(sketch, "E342", {"start": v(54.65, -18.96) * mm, "end": v(51, -19.08) * mm});
            skLineSegment(sketch, "E343", {"start": v(54.03, -30.44) * mm, "end": v(56.53, -27.16) * mm});
            skLineSegment(sketch, "E344", {"start": v(56.91, -19.97) * mm, "end": v(54.65, -18.96) * mm});
            skLineSegment(sketch, "E345", {"start": v(45.95, -45.98) * mm, "end": v(49.52, -47.5) * mm});
            skLineSegment(sketch, "E346", {"start": v(45.95, -45.98) * mm, "end": v(44.73, -54.57) * mm});
            skLineSegment(sketch, "E347", {"start": v(56.53, -27.16) * mm, "end": v(56.91, -19.97) * mm});
            skLineSegment(sketch, "E348", {"start": v(48.3, -55.9) * mm, "end": v(51.9, -56.7) * mm});
            skLineSegment(sketch, "E349", {"start": v(44.73, -54.57) * mm, "end": v(48.3, -55.9) * mm});
            skLineSegment(sketch, "E350", {"start": v(19.08, -3.35) * mm, "end": v(8.32, -3.51) * mm});
            skLineSegment(sketch, "E351", {"start": v(8.83, -20.7) * mm, "end": v(19.08, -20.8) * mm});
            skLineSegment(sketch, "E352", {"start": v(8.32, -3.51) * mm, "end": v(8.83, -20.7) * mm});
            skLineSegment(sketch, "E353", {"start": v(19.08, -20.8) * mm, "end": v(29.32, -20.7) * mm});
            skLineSegment(sketch, "E354", {"start": v(29.32, -20.7) * mm, "end": v(29.83, -3.51) * mm});
            skLineSegment(sketch, "E355", {"start": v(29.83, -3.51) * mm, "end": v(19.08, -3.35) * mm});
            skLineSegment(sketch, "E356", {"start": v(-24.08, 68.13) * mm, "end": v(-24.08, 59.27) * mm});
            skLineSegment(sketch, "E357", {"start": v(-7.21, 59.27) * mm, "end": v(-7.21, 68.94) * mm});
            skLineSegment(sketch, "E358", {"start": v(-7.21, 68.94) * mm, "end": v(-24.08, 68.13) * mm});
            skLineSegment(sketch, "E359", {"start": v(-24.08, 50.41) * mm, "end": v(-7.21, 49.6) * mm});
            skLineSegment(sketch, "E360", {"start": v(-7.21, 49.6) * mm, "end": v(-7.21, 59.27) * mm});
            skLineSegment(sketch, "E361", {"start": v(-24.08, 59.27) * mm, "end": v(-24.08, 50.41) * mm});
            skLineSegment(sketch, "E362", {"start": v(-5.77, 49.11) * mm, "end": v(-5.68, 59.27) * mm});
            skLineSegment(sketch, "E363", {"start": v(-8.57, 42.57) * mm, "end": v(-7.21, 49.6) * mm});
            skLineSegment(sketch, "E364", {"start": v(-23.77, 43.97) * mm, "end": v(-8.57, 42.57) * mm});
            skLineSegment(sketch, "E365", {"start": v(-7.21, 68.94) * mm, "end": v(-8.57, 75.98) * mm});
            skLineSegment(sketch, "E366", {"start": v(-8.57, 75.98) * mm, "end": v(-23.68, 74.58) * mm});
            skLineSegment(sketch, "E367", {"start": v(-23.68, 74.58) * mm, "end": v(-24.08, 68.13) * mm});
            skLineSegment(sketch, "E368", {"start": v(-5.68, 59.27) * mm, "end": v(-5.77, 69.43) * mm});
            skLineSegment(sketch, "E369", {"start": v(-10.83, 36.38) * mm, "end": v(-8.57, 42.57) * mm});
            skLineSegment(sketch, "E370", {"start": v(-14.22, 27.15) * mm, "end": v(-10.83, 36.38) * mm});
            skLineSegment(sketch, "E371", {"start": v(-17.23, 18.86) * mm, "end": v(-14.22, 27.15) * mm});
            skLineSegment(sketch, "E372", {"start": v(-16.57, 11.83) * mm, "end": v(-13.48, 12.46) * mm});
            skLineSegment(sketch, "E373", {"start": v(-13.48, 12.46) * mm, "end": v(-14.3, 16.74) * mm});
            skLineSegment(sketch, "E374", {"start": v(-14.3, 16.74) * mm, "end": v(-17.23, 18.86) * mm});
            skLineSegment(sketch, "E375", {"start": v(-21.46, 21.07) * mm, "end": v(-20.07, 12.2) * mm});
            skLineSegment(sketch, "E376", {"start": v(-15.52, 1) * mm, "end": v(-13.26, 2.43) * mm});
            skLineSegment(sketch, "E377", {"start": v(-13.26, 2.43) * mm, "end": v(-13.44, 10.05) * mm});
            skLineSegment(sketch, "E378", {"start": v(-13.44, 10.05) * mm, "end": v(-16.57, 11.83) * mm});
            skLineSegment(sketch, "E379", {"start": v(-19.9, -0.74) * mm, "end": v(-15.52, 1) * mm});
            skLineSegment(sketch, "E380", {"start": v(-20.07, 12.2) * mm, "end": v(-19.9, -0.74) * mm});
            skLineSegment(sketch, "E381", {"start": v(-16.23, 18.38) * mm, "end": v(-13.01, 26.88) * mm});
            skLineSegment(sketch, "E382", {"start": v(-13, 26.93) * mm, "end": v(-9.48, 36.3) * mm});
            skLineSegment(sketch, "E383", {"start": v(-17.23, 18.86) * mm, "end": v(-16.23, 18.38) * mm});
            skLineSegment(sketch, "E384", {"start": v(-9.49, 36.26) * mm, "end": v(-7.1, 42.58) * mm});
            skLineSegment(sketch, "E385", {"start": v(-9.48, 82.25) * mm, "end": v(-13, 91.61) * mm});
            skLineSegment(sketch, "E386", {"start": v(-14.22, 91.4) * mm, "end": v(-10.83, 82.17) * mm});
            skLineSegment(sketch, "E387", {"start": v(-14.22, 91.4) * mm, "end": v(-17.23, 99.68) * mm});
            skLineSegment(sketch, "E388", {"start": v(-8.57, 75.98) * mm, "end": v(-10.83, 82.17) * mm});
            skLineSegment(sketch, "E389", {"start": v(-15.52, 117.54) * mm, "end": v(-19.9, 119.28) * mm});
            skLineSegment(sketch, "E390", {"start": v(-16.57, 106.71) * mm, "end": v(-13.44, 108.5) * mm});
            skLineSegment(sketch, "E391", {"start": v(-13.44, 108.5) * mm, "end": v(-13.26, 116.11) * mm});
            skLineSegment(sketch, "E392", {"start": v(-13.26, 116.11) * mm, "end": v(-15.52, 117.54) * mm});
            skLineSegment(sketch, "E393", {"start": v(-17.23, 99.68) * mm, "end": v(-14.3, 101.8) * mm});
            skLineSegment(sketch, "E394", {"start": v(-14.3, 101.8) * mm, "end": v(-13.48, 106.09) * mm});
            skLineSegment(sketch, "E395", {"start": v(-13.48, 106.09) * mm, "end": v(-16.57, 106.71) * mm});
            skLineSegment(sketch, "E396", {"start": v(-13.01, 91.67) * mm, "end": v(-16.23, 100.17) * mm});
            skLineSegment(sketch, "E397", {"start": v(-7.1, 75.97) * mm, "end": v(-9.49, 82.29) * mm});
            skLineSegment(sketch, "E398", {"start": v(-16.23, 100.17) * mm, "end": v(-17.23, 99.68) * mm});
            skLineSegment(sketch, "E399", {"start": v(-7.35, 41.75) * mm, "end": v(-5.73, 49.92) * mm});
            skLineSegment(sketch, "E400", {"start": v(-5.73, 68.63) * mm, "end": v(-7.35, 76.8) * mm});
            skLineSegment(sketch, "E401", {"start": v(-52.57, 62.13) * mm, "end": v(-52.57, 59.28) * mm});
            skLineSegment(sketch, "E402", {"start": v(-24.12, 68.13) * mm, "end": v(-52.57, 65.42) * mm});
            skLineSegment(sketch, "E403", {"start": v(-52.57, 65.42) * mm, "end": v(-52.57, 62.13) * mm});
            skLineSegment(sketch, "E404", {"start": v(-52.57, 59.28) * mm, "end": v(-52.57, 56.42) * mm});
            skLineSegment(sketch, "E405", {"start": v(-52.57, 56.42) * mm, "end": v(-52.57, 53.13) * mm});
            skLineSegment(sketch, "E406", {"start": v(-52.57, 53.13) * mm, "end": v(-24.12, 50.42) * mm});
            skLineSegment(sketch, "E407", {"start": v(-52.1, 71.04) * mm, "end": v(-52.57, 65.42) * mm});
            skLineSegment(sketch, "E408", {"start": v(-23.77, 74.58) * mm, "end": v(-52.1, 71.04) * mm});
            skLineSegment(sketch, "E409", {"start": v(-21.48, 97.44) * mm, "end": v(-20.07, 106.28) * mm});
            skLineSegment(sketch, "E410", {"start": v(-47.28, 92.74) * mm, "end": v(-49.48, 84.37) * mm});
            skLineSegment(sketch, "E411", {"start": v(-20.07, 106.28) * mm, "end": v(-19.9, 119.28) * mm});
            skLineSegment(sketch, "E412", {"start": v(-49.48, 84.37) * mm, "end": v(-52.1, 71.04) * mm});
            skLineSegment(sketch, "E413", {"start": v(-23.77, 74.58) * mm, "end": v(-21.48, 97.44) * mm});
            skLineSegment(sketch, "E414", {"start": v(-21.48, 21.11) * mm, "end": v(-23.77, 43.97) * mm});
            skLineSegment(sketch, "E415", {"start": v(-23.77, 43.97) * mm, "end": v(-52.1, 47.5) * mm});
            skLineSegment(sketch, "E416", {"start": v(-52.1, 47.5) * mm, "end": v(-49.48, 34.18) * mm});
            skLineSegment(sketch, "E417", {"start": v(-52.57, 53.13) * mm, "end": v(-52.1, 47.5) * mm});
            skLineSegment(sketch, "E418", {"start": v(-23.77, 43.97) * mm, "end": v(-24.12, 50.42) * mm});
            skLineSegment(sketch, "E419", {"start": v(-40.65, 122.6) * mm, "end": v(-47.28, 92.74) * mm});
            skLineSegment(sketch, "E420", {"start": v(-52.7, -7.04) * mm, "end": v(-55.97, 12.22) * mm});
            skLineSegment(sketch, "E421", {"start": v(-55.97, 12.22) * mm, "end": v(-58.94, 9.22) * mm});
            skLineSegment(sketch, "E422", {"start": v(-52.7, -7.04) * mm, "end": v(-44.62, -5.15) * mm});
            skLineSegment(sketch, "E423", {"start": v(-44.62, -5.15) * mm, "end": v(-40.76, -4.08) * mm});
            skLineSegment(sketch, "E424", {"start": v(-47.1, -10.26) * mm, "end": v(-38.88, -6.07) * mm});
            skLineSegment(sketch, "E425", {"start": v(-38.88, -6.07) * mm, "end": v(-40.76, -4.08) * mm});
            skLineSegment(sketch, "E426", {"start": v(-55.52, -9.1) * mm, "end": v(-56.23, -10.76) * mm});
            skLineSegment(sketch, "E427", {"start": v(-58.94, 9.22) * mm, "end": v(-56.12, -7.74) * mm});
            skLineSegment(sketch, "E428", {"start": v(-58.94, 109.33) * mm, "end": v(-55.97, 106.33) * mm});
            skLineSegment(sketch, "E429", {"start": v(-55.97, 106.33) * mm, "end": v(-52.7, 125.59) * mm});
            skLineSegment(sketch, "E430", {"start": v(-55.97, 106.33) * mm, "end": v(-49.02, 98.4) * mm});
            skLineSegment(sketch, "E431", {"start": v(-44.62, 123.7) * mm, "end": v(-52.7, 125.59) * mm});
            skLineSegment(sketch, "E432", {"start": v(-49.02, 98.4) * mm, "end": v(-47.28, 92.74) * mm});
            skLineSegment(sketch, "E433", {"start": v(-40.65, 122.6) * mm, "end": v(-44.62, 123.7) * mm});
            skLineSegment(sketch, "E434", {"start": v(-38.42, 124.28) * mm, "end": v(-47.1, 128.81) * mm});
            skLineSegment(sketch, "E435", {"start": v(-56.23, 129.3) * mm, "end": v(-56.12, 126.3) * mm});
            skLineSegment(sketch, "E436", {"start": v(-56.12, 126.3) * mm, "end": v(-58.94, 109.33) * mm});
            skLineSegment(sketch, "E437", {"start": v(-56.12, -7.74) * mm, "end": v(-55.52, -9.1) * mm});
            skLineSegment(sketch, "E438", {"start": v(-34.94, -9.76) * mm, "end": v(-34.39, -10.16) * mm});
            skLineSegment(sketch, "E439", {"start": v(-32.4, -11.18) * mm, "end": v(-31.75, -11.39) * mm});
            skLineSegment(sketch, "E440", {"start": v(-29.53, -11.74) * mm, "end": v(-28.85, -11.74) * mm});
            skLineSegment(sketch, "E441", {"start": v(-26.64, -11.39) * mm, "end": v(-26, -11.18) * mm});
            skLineSegment(sketch, "E442", {"start": v(-23.95, -10.12) * mm, "end": v(-23.44, -9.76) * mm});
            skLineSegment(sketch, "E443", {"start": v(-21.86, -8.17) * mm, "end": v(-21.46, -7.62) * mm});
            skLineSegment(sketch, "E444", {"start": v(-20.44, -5.63) * mm, "end": v(-20.23, -4.98) * mm});
            skLineSegment(sketch, "E445", {"start": v(-56.23, -10.76) * mm, "end": v(-47.1, -10.26) * mm});
            skLineSegment(sketch, "E446", {"start": v(-55.97, 12.22) * mm, "end": v(-49.02, 20.16) * mm});
            skLineSegment(sketch, "E447", {"start": v(-49.48, 34.18) * mm, "end": v(-47.28, 25.81) * mm});
            skLineSegment(sketch, "E448", {"start": v(-49.02, 20.16) * mm, "end": v(-47.28, 25.81) * mm});
            skLineSegment(sketch, "E449", {"start": v(-39.7, -5) * mm, "end": v(-40.76, -4.08) * mm});
            skLineSegment(sketch, "E450", {"start": v(-7.58, -60.84) * mm, "end": v(-2.88, -61.83) * mm});
            skLineSegment(sketch, "E451", {"start": v(-13.2, -59.66) * mm, "end": v(-7.58, -60.84) * mm});
            skLineSegment(sketch, "E452", {"start": v(-20.2, -66.03) * mm, "end": v(-13.2, -59.66) * mm});
            skLineSegment(sketch, "E453", {"start": v(-21.8, -68.8) * mm, "end": v(-22.06, -79.95) * mm});
            skLineSegment(sketch, "E454", {"start": v(-39.13, -68.4) * mm, "end": v(-33.25, -68.54) * mm});
            skLineSegment(sketch, "E455", {"start": v(-0.96, -96.88) * mm, "end": v(2.2, -95.72) * mm});
            skLineSegment(sketch, "E456", {"start": v(-4.17, -88.7) * mm, "end": v(-8.94, -89.22) * mm});
            skLineSegment(sketch, "E457", {"start": v(-14.66, -89.85) * mm, "end": v(-3.47, -99.36) * mm});
            skLineSegment(sketch, "E458", {"start": v(-3.47, -99.36) * mm, "end": v(3.92, -105.64) * mm});
            skLineSegment(sketch, "E459", {"start": v(-28.7, -91.67) * mm, "end": v(-20.94, -91.92) * mm});
            skLineSegment(sketch, "E460", {"start": v(-27.18, -115.72) * mm, "end": v(-28.91, -126.27) * mm});
            skLineSegment(sketch, "E461", {"start": v(-39.13, -68.4) * mm, "end": v(-39.38, -79.55) * mm});
            skLineSegment(sketch, "E462", {"start": v(-39.38, -79.55) * mm, "end": v(-33.5, -79.68) * mm});
            skLineSegment(sketch, "E463", {"start": v(-37.6, 125.01) * mm, "end": v(-36, 126.48) * mm});
            skLineSegment(sketch, "E464", {"start": v(-36, 126.48) * mm, "end": v(-33.98, 128.21) * mm});
            skLineSegment(sketch, "E465", {"start": v(-33.98, 128.21) * mm, "end": v(-31.54, 129.24) * mm});
            skLineSegment(sketch, "E466", {"start": v(-31.54, 129.24) * mm, "end": v(-28.9, 129.45) * mm});
            skLineSegment(sketch, "E467", {"start": v(-28.9, 129.45) * mm, "end": v(-26.32, 128.84) * mm});
            skLineSegment(sketch, "E468", {"start": v(-26.32, 128.84) * mm, "end": v(-24.05, 127.47) * mm});
            skLineSegment(sketch, "E469", {"start": v(-24.05, 127.47) * mm, "end": v(-22.32, 125.46) * mm});
            skLineSegment(sketch, "E470", {"start": v(-39.23, 123.54) * mm, "end": v(-37.6, 125.01) * mm});
            skLineSegment(sketch, "E471", {"start": v(-56.23, 129.3) * mm, "end": v(-47.1, 128.81) * mm});
            skSolve(sketch);
        }
        {
            var Q0;
            Q0=makeQuery(id+"F0.imprint","IMPRINT",FACE,{"disambiguationData":[TD([[makeQuery(id+"F0.imprint","IMPRINT",EDGE,{"derivedFrom":sQuery(id+"F0.wireOp",EDGE,"E300")}),1.0]])]});
            extrude(context, id + "F1", {"entities" : qUnion([Q0]), "depth" : 12.7 * mm, "offsetDistance" : 25.4 * mm});
        }
        {
            var Q0;
            Q0=makeQuery(id+"F0.imprint","IMPRINT",FACE,{"disambiguationData":[TD([[makeQuery(id+"F0.imprint","IMPRINT",EDGE,{"derivedFrom":sQuery(id+"F0.wireOp",EDGE,"E351")}),1.0]])]});
            extrude(context, id + "F2", {"entities" : qUnion([Q0]), "depth" : 12.7 * mm, "offsetDistance" : 25.4 * mm});
        }
        {
            var Q0;
            {var subQ4=sQuery(id+"F0.wireOp",EDGE,"E283");Q0=makeQuery(id+"F0.imprint","IMPRINT",FACE,{"disambiguationData":[TD([[makeQuery(id+"F0.imprint","IMPRINT",EDGE,{"derivedFrom":subQ4}),1.0]])]});}
            extrude(context, id + "F3", {"entities" : qUnion([Q0]), "operationType" : NewBodyOperationType.ADD, "depth" : 12.7 * mm, "offsetDistance" : 25.4 * mm});
        }
    });
